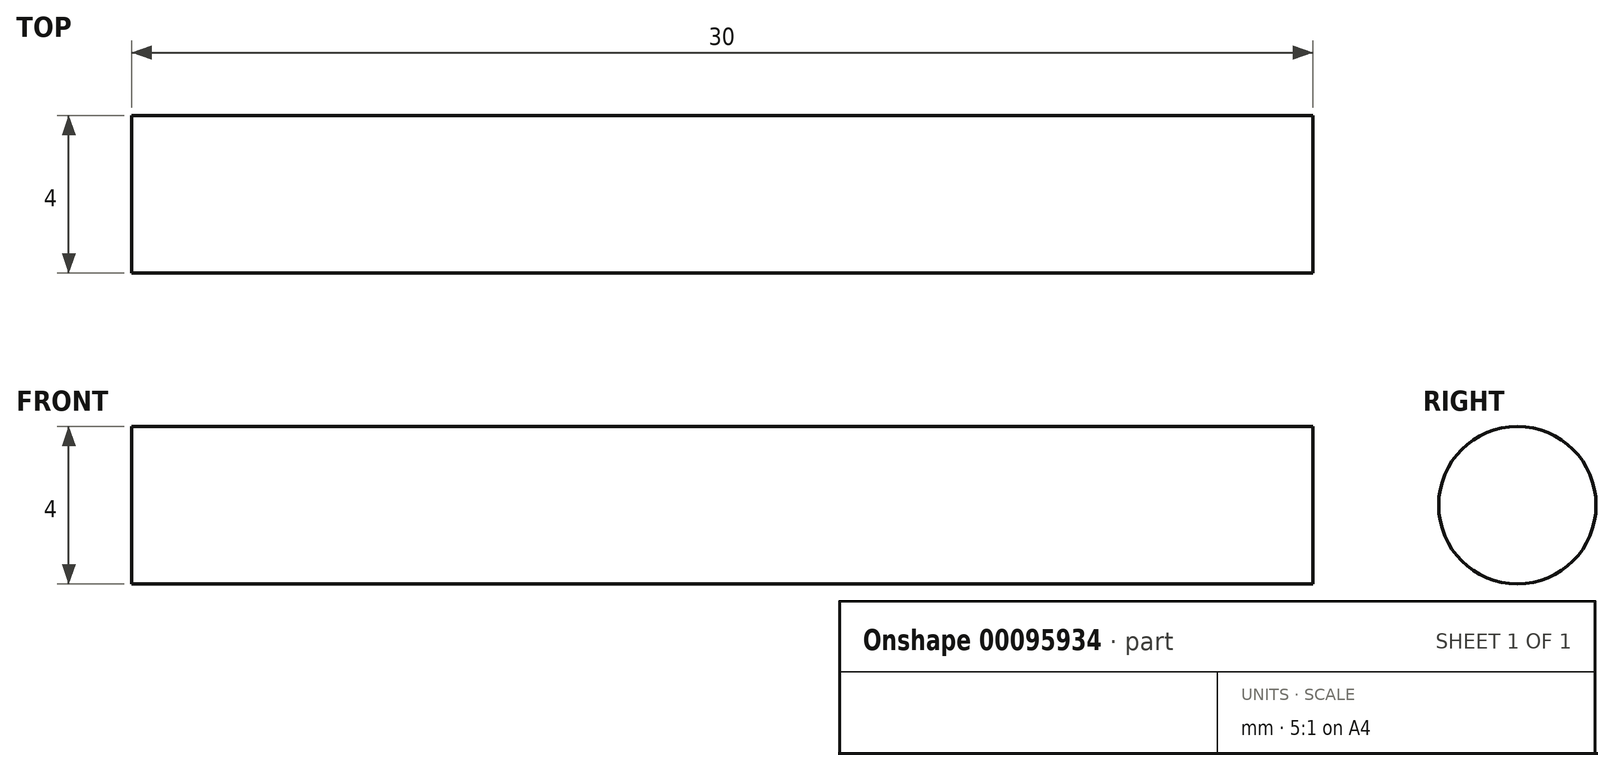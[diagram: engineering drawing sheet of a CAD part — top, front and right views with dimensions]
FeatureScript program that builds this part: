
annotation { "Feature Type Name" : "Feature", "Feature Type Description" : "" }
export const myFeature = defineFeature(function(context is Context, id is Id, definition is map)
    precondition{}
    {
        {
            var Q0;
            Q0=qCreatedBy(makeId("Right.planeOp"),FACE);
            var sketch = newSketch(context, id + "F0", { "sketchPlane" : qUnion([Q0])});
            skCircle(sketch, "E0", {"center": v(0, 0) * mm, "radius": 2 * mm});
            skSolve(sketch);
        }
        {
            var Q0;
            Q0 = qSketchRegion(id + "F0", true);
            extrude(context, id + "F1", {"entities" : qUnion([Q0]), "depth" : 30 * mm});
        }
    });
